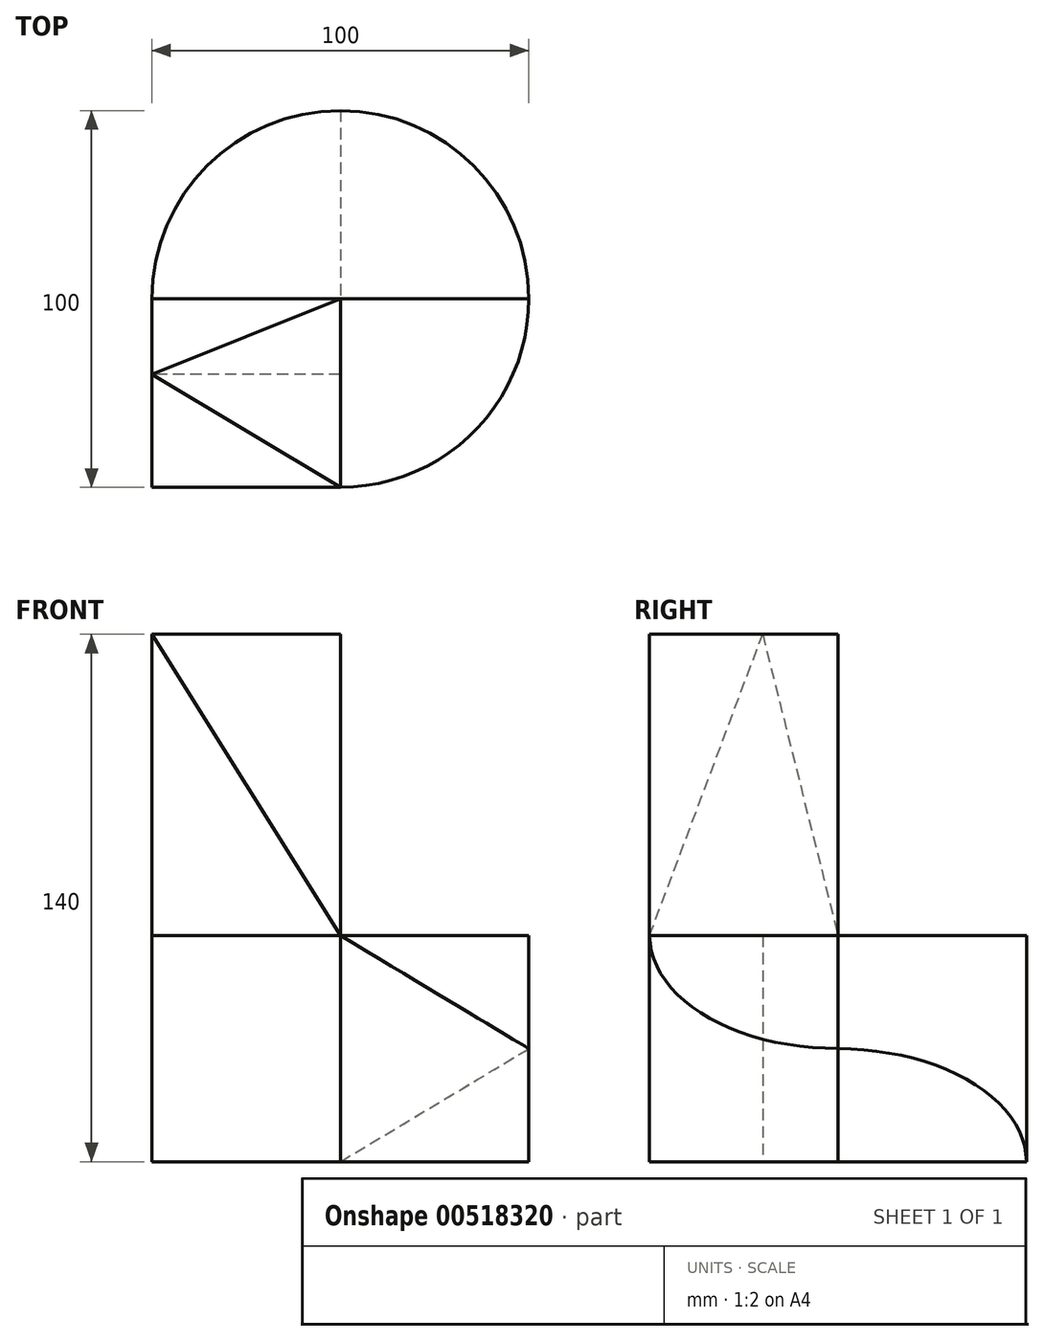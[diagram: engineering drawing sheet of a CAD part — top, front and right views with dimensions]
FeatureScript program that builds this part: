
annotation { "Feature Type Name" : "Feature", "Feature Type Description" : "" }
export const myFeature = defineFeature(function(context is Context, id is Id, definition is map)
    precondition{}
    {
        {
            var Q0;
            Q0=qCreatedBy(makeId("Top.planeOp"),FACE);
            var sketch = newSketch(context, id + "F0", { "sketchPlane" : qUnion([Q0])});
            skLineSegment(sketch, "E0.bottom", {"start": v(0, 0) * mm, "end": v(100, 0) * mm});
            skLineSegment(sketch, "E0.top", {"start": v(0, 100) * mm, "end": v(100, 100) * mm});
            skLineSegment(sketch, "E0.left", {"start": v(0, 0) * mm, "end": v(0, 100) * mm});
            skLineSegment(sketch, "E0.right", {"start": v(100, 0) * mm, "end": v(100, 100) * mm});
            skSolve(sketch);
        }
        {
            var Q0;
            Q0 = qSketchRegion(id + "F0", true);
            extrude(context, id + "F1", {"entities" : qUnion([Q0]), "depth" : 140 * mm, "offsetDistance" : 25 * mm});
        }
        {
            var Q0;
            Q0=makeQuery(id+"F1.opExtrude","CAP_FACE",FACE,{"disambiguationData":[OSD([sQuery(id+"F0.wireOp",EDGE,"E0.bottom"),sQuery(id+"F0.wireOp",EDGE,"E0.top"),sQuery(id+"F0.wireOp",EDGE,"E0.left"),sQuery(id+"F0.wireOp",EDGE,"E0.right")])],"isStart":false});
            var sketch = newSketch(context, id + "F2", { "sketchPlane" : qUnion([Q0])});
            skCircle(sketch, "E1", {"center": v(50, 50) * mm, "radius": 50 * mm});
            skSolve(sketch);
        }
        {
            var Q0;
            {var subQ0=sQuery(id+"F2.wireOp",EDGE,"E1");var subQ1=makeQuery(id+"F1.opExtrude","CAP_EDGE",EDGE,{"disambiguationData":[OSD([sQuery(id+"F0.wireOp",EDGE,"E0.top")])],"isStart":false});var subQ2=makeQuery(id+"F2.imprint","INTERSECT",VERTEX,{"derivedFrom":[subQ1,subQ0]});Q0=makeQuery(id+"F2.imprint","IMPRINT",FACE,{"disambiguationData":[TD([[makeQuery(id+"F2.imprint","IMPRINT",EDGE,{"disambiguationData":[TD([[subQ2,-1.0]])],"derivedFrom":subQ0}),-1.0]])]});}
            var Q1;
            {var subQ0=sQuery(id+"F2.wireOp",EDGE,"E1");var subQ1=makeQuery(id+"F1.opExtrude","CAP_EDGE",EDGE,{"disambiguationData":[OSD([sQuery(id+"F0.wireOp",EDGE,"E0.top")])],"isStart":false});var subQ2=makeQuery(id+"F2.imprint","INTERSECT",VERTEX,{"derivedFrom":[subQ1,subQ0]});Q1=makeQuery(id+"F2.imprint","IMPRINT",FACE,{"disambiguationData":[TD([[makeQuery(id+"F2.imprint","IMPRINT",EDGE,{"disambiguationData":[TD([[subQ2,1.0]])],"derivedFrom":subQ0}),-1.0]])]});}
            var Q2;
            {var subQ0=sQuery(id+"F2.wireOp",EDGE,"E1");var subQ1=makeQuery(id+"F1.opExtrude","CAP_EDGE",EDGE,{"disambiguationData":[OSD([sQuery(id+"F0.wireOp",EDGE,"E0.right")])],"isStart":false});var subQ2=makeQuery(id+"F2.imprint","INTERSECT",VERTEX,{"derivedFrom":[subQ1,subQ0]});Q2=makeQuery(id+"F2.imprint","IMPRINT",FACE,{"disambiguationData":[TD([[makeQuery(id+"F2.imprint","IMPRINT",EDGE,{"disambiguationData":[TD([[subQ2,1.0]])],"derivedFrom":subQ0}),-1.0]])]});}
            extrude(context, id + "F3", {"entities" : qUnion([Q0, Q1, Q2]), "operationType" : NewBodyOperationType.REMOVE, "endBound" : BoundingType.THROUGH_ALL, "oppositeDirection" : true, "depth" : 25 * mm, "offsetDistance" : 25 * mm});
        }
        {
            var Q0;
            Q0=makeQuery(id+"F1.opExtrude","CAP_FACE",FACE,{"disambiguationData":[OSD([sQuery(id+"F0.wireOp",EDGE,"E0.bottom"),sQuery(id+"F0.wireOp",EDGE,"E0.top"),sQuery(id+"F0.wireOp",EDGE,"E0.left"),sQuery(id+"F0.wireOp",EDGE,"E0.right")])],"isStart":false});
            var sketch = newSketch(context, id + "F4", { "sketchPlane" : qUnion([Q0])});
            skLineSegment(sketch, "E2.bottom", {"start": v(0, 0) * mm, "end": v(50, 0) * mm});
            skLineSegment(sketch, "E2.top", {"start": v(0, 50) * mm, "end": v(50, 50) * mm});
            skLineSegment(sketch, "E2.left", {"start": v(0, 0) * mm, "end": v(0, 50) * mm});
            skLineSegment(sketch, "E2.right", {"start": v(50, 0) * mm, "end": v(50, 50) * mm});
            skSolve(sketch);
        }
        {
            var Q0;
            Q0=makeQuery(id+"F4.imprint","IMPRINT",FACE,{"disambiguationData":[TD([[makeQuery(id+"F4.imprint","IMPRINT",EDGE,{"derivedFrom":sQuery(id+"F4.wireOp",EDGE,"E2.top")}),1.0]])]});
            extrude(context, id + "F5", {"entities" : qUnion([Q0]), "operationType" : NewBodyOperationType.REMOVE, "oppositeDirection" : true, "depth" : 80 * mm, "offsetDistance" : 25 * mm});
        }
        {
            var Q0;
            Q0=makeQuery(id+"F1.opExtrude","CAP_FACE",FACE,{"disambiguationData":[OSD([sQuery(id+"F0.wireOp",EDGE,"E0.bottom"),sQuery(id+"F0.wireOp",EDGE,"E0.top"),sQuery(id+"F0.wireOp",EDGE,"E0.left"),sQuery(id+"F0.wireOp",EDGE,"E0.right")])],"isStart":false});
            var sketch = newSketch(context, id + "F6", { "sketchPlane" : qUnion([Q0])});
            skLineSegment(sketch, "E3", {"start": v(50, 50) * mm, "end": v(0, 30) * mm});
            skLineSegment(sketch, "E4", {"start": v(0, 30) * mm, "end": v(50, 0) * mm});
            skLineSegment(sketch, "E5", {"start": v(0, 30) * mm, "end": v(50, 30) * mm});
            skSolve(sketch);
        }
        {
            var Q0;
            Q0=makeQuery(id+"F1.opExtrude","SWEPT_FACE",FACE,{"disambiguationData":[OSD([sQuery(id+"F0.wireOp",EDGE,"E0.bottom")])]});
            var sketch = newSketch(context, id + "F7", { "sketchPlane" : qUnion([Q0])});
            skLineSegment(sketch, "E6", {"start": v(50, 60) * mm, "end": v(0, 60) * mm});
            skSolve(sketch);
        }
        {
            var Q0;
            Q0=makeQuery(id+"F1.opExtrude","SWEPT_FACE",FACE,{"disambiguationData":[OSD([sQuery(id+"F0.wireOp",EDGE,"E0.left")])]});
            var sketch = newSketch(context, id + "F8", { "sketchPlane" : qUnion([Q0])});
            skLineSegment(sketch, "E7", {"start": v(0, 60) * mm, "end": v(-30, 140) * mm});
            skSolve(sketch);
        }
        {
            var Q1;
            {var subQ0=sQuery(id+"F7.wireOp",EDGE,"E6");Q1=makeQuery(id+"F7.imprint","IMPRINT",FACE,{"disambiguationData":[TD([[makeQuery(id+"F7.imprint","IMPRINT",EDGE,{"derivedFrom":subQ0}),-1.0]])]});}
            var Q2;
            Q2=sQuery(id+"F8.wireOp",VERTEX,"E7.end");
            loft(context, id + "F9", {"operationType" : NewBodyOperationType.REMOVE, "sheetProfilesArray" : [{ "sheetProfileEntities" : qUnion([Q1]) }, { "sheetProfileEntities" : qUnion([Q2]) }]});
        }
        {
            var Q1;
            {var subQ0=sQuery(id+"F6.wireOp",EDGE,"E3");Q1=makeQuery(id+"F6.imprint","IMPRINT",FACE,{"disambiguationData":[TD([[makeQuery(id+"F6.imprint","IMPRINT",EDGE,{"derivedFrom":subQ0}),-1.0]])]});}
            var Q2;
            Q2=makeQuery(id+"F5.boolean.opBoolean","COPY",VERTEX,{"derivedFrom":makeQuery(id+"F5.opExtrude","CAP_VERTEX",VERTEX,{"disambiguationData":[OSD([sQuery(id+"F4.wireOp",EDGE,"E2.top"),sQuery(id+"F4.wireOp",EDGE,"E2.right")])],"isStart":false})});
            loft(context, id + "F10", {"operationType" : NewBodyOperationType.REMOVE, "sheetProfilesArray" : [{ "sheetProfileEntities" : qUnion([Q1]) }, { "sheetProfileEntities" : qUnion([Q2]) }]});
        }
        {
            var Q0;
            {var subQ0=sQuery(id+"F4.wireOp",EDGE,"E2.right");var subQ1=sQuery(id+"F4.wireOp",EDGE,"E2.top");Q0=makeQuery(id+"F10.boolean.opBoolean","MERGE",VERTEX,{"derivedFrom":[makeQuery(id+"F5.boolean.opBoolean","COPY",VERTEX,{"derivedFrom":makeQuery(id+"F5.opExtrude","CAP_VERTEX",VERTEX,{"disambiguationData":[OSD([subQ1,subQ0])],"isStart":true})}),makeQuery(id+"F10.opLoft","MID_CAP_VERTEX",VERTEX,{"disambiguationData":[OSD([subQ1,subQ0,sQuery(id+"F6.wireOp",EDGE,"E3")])],"capPos":0.0})]});}
            var Q1;
            {var subQ0=sQuery(id+"F4.wireOp",EDGE,"E2.right");var subQ1=sQuery(id+"F4.wireOp",EDGE,"E2.top");Q1=makeQuery(id+"F10.boolean.opBoolean","MERGE",VERTEX,{"derivedFrom":[makeQuery(id+"F5.boolean.opBoolean","COPY",VERTEX,{"derivedFrom":makeQuery(id+"F5.opExtrude","CAP_VERTEX",VERTEX,{"disambiguationData":[OSD([subQ1,subQ0])],"isStart":false})}),makeQuery(id+"F10.opLoft","SWEPT_VERTEX",VERTEX,{"disambiguationData":[OSD([subQ1,subQ0,sQuery(id+"F6.wireOp",EDGE,"E3")])]})]});}
            var Q2;
            {var subQ0=sQuery(id+"F4.wireOp",EDGE,"E2.top");var subQ1=sQuery(id+"F0.wireOp",EDGE,"E0.left");var subQ2=sQuery(id+"F2.wireOp",EDGE,"E1");Q2=makeQuery(id+"F10.boolean.opBoolean","MERGE",VERTEX,{"derivedFrom":[makeQuery(id+"F5.boolean.opBoolean","MERGE",VERTEX,{"derivedFrom":[makeQuery(id+"F3.boolean.opBoolean","COPY",VERTEX,{"derivedFrom":makeQuery(id+"F3.opExtrude","CAP_VERTEX",VERTEX,{"disambiguationData":[OSD([subQ1,subQ2])],"isStart":true})}),makeQuery(id+"F5.opExtrude","CAP_VERTEX",VERTEX,{"disambiguationData":[OSD([subQ2,subQ0,sQuery(id+"F4.wireOp",EDGE,"E2.left")])],"isStart":true})]}),makeQuery(id+"F10.opLoft","MID_CAP_VERTEX",VERTEX,{"disambiguationData":[OSD([subQ1,subQ0])],"capPos":0.0})]});}
            cPlane(context, id + "F11", {"entities" : qUnion([Q0, Q1, Q2]), "cplaneType" : CPlaneType.THREE_POINT, "offset" : 25 * mm, "width" : 150 * mm, "height" : 150 * mm});
        }
        {
            var Q0;
            Q0=qCreatedBy(id+"F11.planeOp",FACE);
            var sketch = newSketch(context, id + "F12", { "sketchPlane" : qUnion([Q0])});
            skLineSegment(sketch, "E8", {"start": v(50, 60) * mm, "end": v(100, 60) * mm});
            skLineSegment(sketch, "E9", {"start": v(100, 60) * mm, "end": v(100, 30) * mm});
            skLineSegment(sketch, "E10", {"start": v(100, 30) * mm, "end": v(50, 60) * mm});
            skSolve(sketch);
        }
        {
            var Q0;
            Q0 = qSketchRegion(id + "F12", true);
            extrude(context, id + "F13", {"entities" : qUnion([Q0]), "operationType" : NewBodyOperationType.REMOVE, "endBound" : BoundingType.UP_TO_NEXT, "depth" : 25 * mm, "offsetDistance" : 25 * mm});
        }
        {
            var Q0;
            Q0=qCreatedBy(id+"F11.planeOp",FACE);
            var sketch = newSketch(context, id + "F14", { "sketchPlane" : qUnion([Q0])});
            skLineSegment(sketch, "E11", {"start": v(100, 29.99) * mm, "end": v(100, 0) * mm});
            skLineSegment(sketch, "E12", {"start": v(100, 0) * mm, "end": v(50, 0) * mm});
            skLineSegment(sketch, "E13", {"start": v(50, 0) * mm, "end": v(100, 29.99) * mm});
            skSolve(sketch);
        }
        {
            var Q0;
            Q0 = qSketchRegion(id + "F14", true);
            extrude(context, id + "F15", {"entities" : qUnion([Q0]), "operationType" : NewBodyOperationType.REMOVE, "endBound" : BoundingType.UP_TO_NEXT, "oppositeDirection" : true, "depth" : 25 * mm, "offsetDistance" : 25 * mm});
        }
        {
            var Q0;
            Q0=makeQuery(id+"F1.opExtrude","SWEPT_FACE",FACE,{"disambiguationData":[OSD([sQuery(id+"F0.wireOp",EDGE,"E0.left")])]});
            var sketch = newSketch(context, id + "F16", { "sketchPlane" : qUnion([Q0])});
            skLineSegment(sketch, "E14", {"start": v(-30, 140) * mm, "end": v(-30, 0) * mm});
            skLineSegment(sketch, "E15", {"start": v(-50, 60) * mm, "end": v(0, 60) * mm});
            skSolve(sketch);
        }
        {
            var Q0;
            {var subQ0=sQuery(id+"F16.wireOp",EDGE,"E14");var subQ1=sQuery(id+"F0.wireOp",EDGE,"E0.left");var subQ2=makeQuery(id+"F1.opExtrude","CAP_EDGE",EDGE,{"disambiguationData":[OSD([subQ1])],"isStart":true});var subQ3=makeQuery(id+"F16.imprint","INTERSECT",VERTEX,{"derivedFrom":[subQ2,subQ0]});Q0=makeQuery(id+"F16.imprint","IMPRINT",FACE,{"disambiguationData":[TD([[makeQuery(id+"F16.imprint","IMPRINT",EDGE,{"disambiguationData":[TD([[subQ3,1.0]])],"derivedFrom":subQ0}),1.0]])]});}
            extrude(context, id + "F17", {"entities" : qUnion([Q0]), "operationType" : NewBodyOperationType.REMOVE, "oppositeDirection" : true, "depth" : 50 * mm, "offsetDistance" : 25 * mm});
        }
    });
